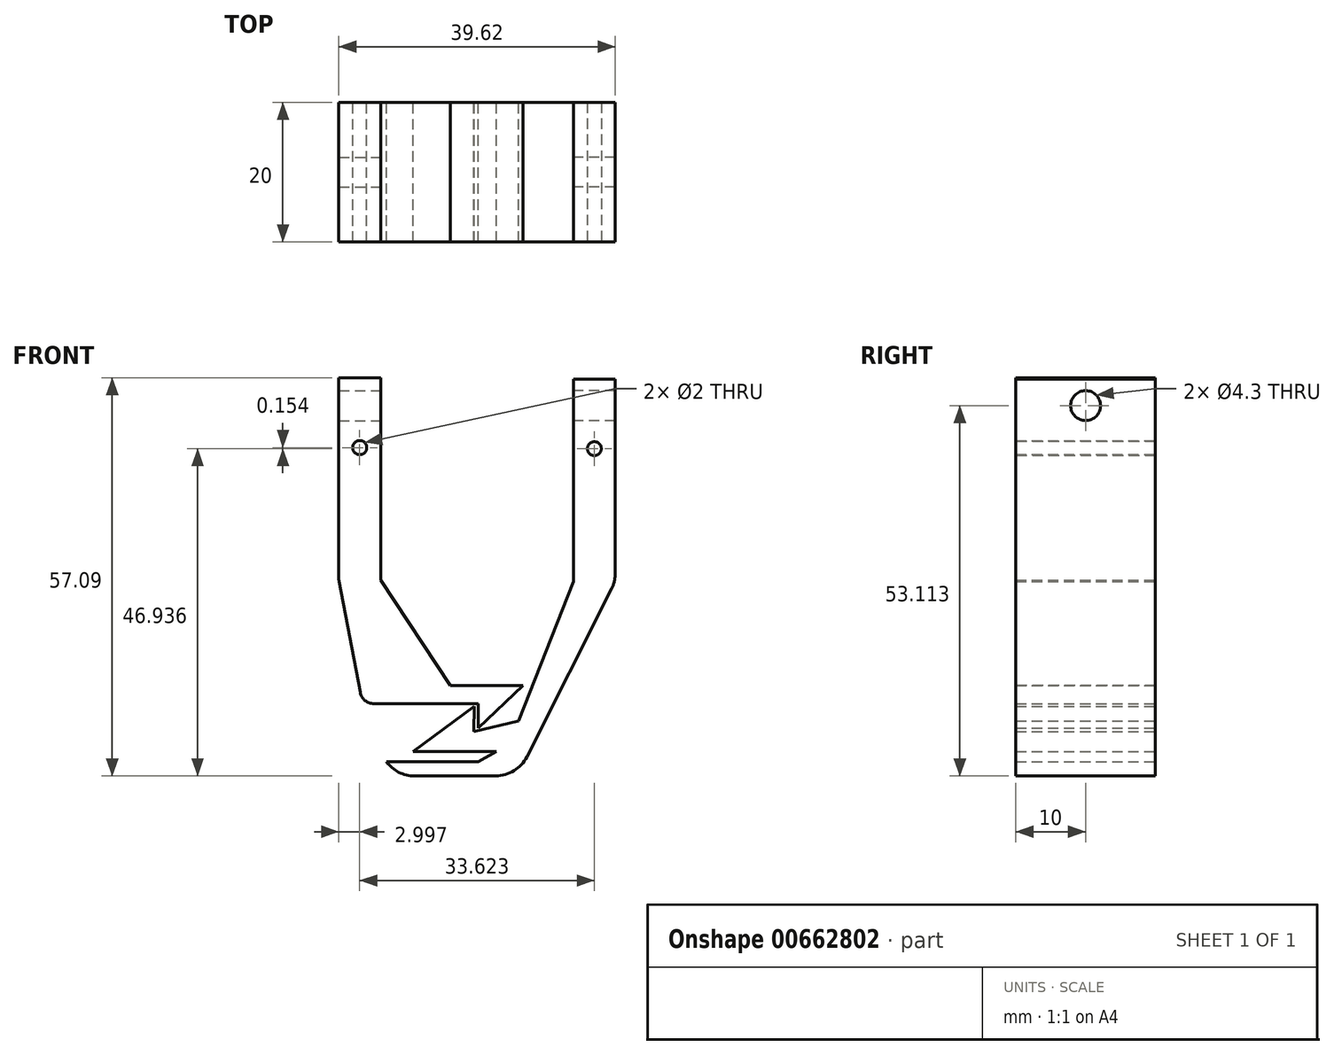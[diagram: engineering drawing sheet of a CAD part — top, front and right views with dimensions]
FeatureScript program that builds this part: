
annotation { "Feature Type Name" : "Feature", "Feature Type Description" : "" }
export const myFeature = defineFeature(function(context is Context, id is Id, definition is map)
    precondition{}
    {
        {
            var Q0;
            Q0=qCreatedBy(makeId("Front.planeOp"),FACE);
            var sketch = newSketch(context, id + "F0", { "sketchPlane" : qUnion([Q0])});
            skLineSegment(sketch, "E0.bottom", {"start": v(-14, 0) * mm, "end": v(-20, 0) * mm});
            skLineSegment(sketch, "E0.top", {"start": v(-14, 29) * mm, "end": v(-20, 29) * mm});
            skLineSegment(sketch, "E0.left", {"start": v(-14, 0) * mm, "end": v(-14, 29) * mm});
            skLineSegment(sketch, "E0.right", {"start": v(-20, 0) * mm, "end": v(-20, 29) * mm});
            skLineSegment(sketch, "E1", {"start": v(0, -15.13) * mm, "end": v(-4.04, -15.13) * mm});
            skLineSegment(sketch, "E2", {"start": v(-14, 0) * mm, "end": v(-4.04, -15.13) * mm});
            skLineSegment(sketch, "E3", {"start": v(-4.05, -17.72) * mm, "end": v(-20, 0) * mm});
            skLineSegment(sketch, "E4", {"start": v(-4.05, -17.72) * mm, "end": v(0, -17.72) * mm});
            skLineSegment(sketch, "E5", {"start": v(0, -17.72) * mm, "end": v(0, -21.21) * mm});
            skLineSegment(sketch, "E6", {"start": v(0, -15.13) * mm, "end": v(6.4, -15.13) * mm});
            skLineSegment(sketch, "E7", {"start": v(6.4, -15.13) * mm, "end": v(0, -21.21) * mm});
            skLineSegment(sketch, "E8", {"start": v(-20, 0) * mm, "end": v(-16.63, -17.72) * mm});
            skLineSegment(sketch, "E9", {"start": v(-16.63, -17.72) * mm, "end": v(-4.05, -17.72) * mm});
            skPoint(sketch, "E10", {"position": v(-17, 19) * mm});
            skSolve(sketch);
        }
        {
            var Q0;
            Q0=qSketchRegion(id+"F0",true);
            extrude(context, id + "F1", {"entities" : qUnion([Q0]), "depth" : 20 * mm, "offsetDistance" : 25 * mm, "symmetric" : true});
        }
        {
            var Q0;
            Q0=qCreatedBy(makeId("Front.planeOp"),FACE);
            var sketch = newSketch(context, id + "F2", { "sketchPlane" : qUnion([Q0])});
            skLineSegment(sketch, "E11.MirrorCS", {"start": v(19.62, -0.19) * mm, "end": v(19.62, 26.84) * mm});
            skLineSegment(sketch, "E12.MirrorCS", {"start": v(13.62, -0.19) * mm, "end": v(13.62, 26.84) * mm});
            skLineSegment(sketch, "E13.MirrorCS", {"start": v(13.62, -0.19) * mm, "end": v(19.62, -0.19) * mm});
            skLineSegment(sketch, "E14", {"start": v(5.79, -20.18) * mm, "end": v(-0.63, -21.74) * mm});
            skLineSegment(sketch, "E15", {"start": v(5.79, -20.18) * mm, "end": v(5.79, -24.57) * mm});
            skLineSegment(sketch, "E16", {"start": v(5.79, -24.57) * mm, "end": v(-0.66, -24.57) * mm});
            skLineSegment(sketch, "E17", {"start": v(-0.66, -24.57) * mm, "end": v(-0.62, -20.18) * mm});
            skLineSegment(sketch, "E18", {"start": v(-0.62, -18.1) * mm, "end": v(-0.63, -21.74) * mm});
            skLineSegment(sketch, "E19", {"start": v(13.62, -0.19) * mm, "end": v(5.79, -20.18) * mm});
            skLineSegment(sketch, "E20", {"start": v(-0.66, -24.57) * mm, "end": v(-9.38, -24.57) * mm});
            skLineSegment(sketch, "E21", {"start": v(-9.38, -24.57) * mm, "end": v(-0.62, -18.1) * mm});
            skLineSegment(sketch, "E22", {"start": v(5.56, -28.09) * mm, "end": v(-13.19, -28.09) * mm});
            skLineSegment(sketch, "E23", {"start": v(-13.19, -28.09) * mm, "end": v(-13.19, -26.04) * mm});
            skLineSegment(sketch, "E24", {"start": v(-13.19, -26.04) * mm, "end": v(0, -26.04) * mm});
            skLineSegment(sketch, "E25", {"start": v(0, -26.04) * mm, "end": v(2.57, -24.57) * mm});
            skLineSegment(sketch, "E26", {"start": v(19.62, 26.84) * mm, "end": v(19.62, 28.85) * mm});
            skLineSegment(sketch, "E27", {"start": v(13.62, 26.84) * mm, "end": v(13.62, 28.85) * mm});
            skLineSegment(sketch, "E28", {"start": v(13.62, 28.85) * mm, "end": v(19.62, 28.85) * mm});
            skPoint(sketch, "E29", {"position": v(16.62, 18.85) * mm});
            skLineSegment(sketch, "E30", {"start": v(19.62, -0.19) * mm, "end": v(5.56, -28.09) * mm});
            skLineSegment(sketch, "E31", {"start": v(16.62, 28.85) * mm, "end": v(16.62, 22.82) * mm});
            skSolve(sketch);
        }
        {
            var Q0;
            Q0 = qSketchRegion(id + "F2", true);
            extrude(context, id + "F3", {"entities" : qUnion([Q0]), "depth" : 20 * mm, "offsetDistance" : 25 * mm, "symmetric" : true});
        }
        {
            var Q0;
            Q0=makeQuery(id+"F3.opExtrude","SWEPT_EDGE",EDGE,{"disambiguationData":[OSD([sQuery(id+"F2.wireOp",EDGE,"du4RMWLr-ao0C-ay0E-4CYy-pwUNnrK6PciY"),sQuery(id+"F2.wireOp",EDGE,"E22")])]});
            fillet(context, id + "F4", {"entities" : qUnion([Q0]), "radius" : 5 * mm, "tangentPropagation" : true, "allowEdgeOverflow" : false});
        }
        {
            var Q0;
            Q0=makeQuery(id+"F1.opExtrude","SWEPT_EDGE",EDGE,{"disambiguationData":[OSD([sQuery(id+"F0.wireOp",EDGE,"E8"),sQuery(id+"F0.wireOp",EDGE,"E9")])]});
            fillet(context, id + "F5", {"entities" : qUnion([Q0]), "radius" : 2 * mm, "tangentPropagation" : true, "allowEdgeOverflow" : false});
        }
        {
            var Q0;
            Q0=makeQuery(id+"F1.opExtrude","SWEPT_EDGE",EDGE,{"disambiguationData":[OSD([sQuery(id+"F0.wireOp",EDGE,"E0.bottom"),sQuery(id+"F0.wireOp",EDGE,"E0.right"),sQuery(id+"F0.wireOp",EDGE,"E3"),sQuery(id+"F0.wireOp",EDGE,"E8")])]});
            fillet(context, id + "F6", {"entities" : qUnion([Q0]), "radius" : 2 * mm, "tangentPropagation" : true, "allowEdgeOverflow" : false});
        }
        {
            var Q0;
            Q0=makeQuery(id+"F3.opExtrude","SWEPT_EDGE",EDGE,{"disambiguationData":[OSD([sQuery(id+"F2.wireOp",EDGE,"E11.MirrorCS"),sQuery(id+"F2.wireOp",EDGE,"E13.MirrorCS"),sQuery(id+"F2.wireOp",EDGE,"409ef352-82fb-4545-b7b6-5d9b69b97d5a")])]});
            fillet(context, id + "F7", {"entities" : qUnion([Q0]), "radius" : 5 * mm, "tangentPropagation" : true, "allowEdgeOverflow" : false});
        }
        {
            var Q0;
            Q0=qCreatedBy(makeId("Right.planeOp"),FACE);
            var sketch = newSketch(context, id + "F8", { "sketchPlane" : qUnion([Q0])});
            skPoint(sketch, "E32", {"position": v(0, 25.02) * mm});
            skSolve(sketch);
        }
        {
            var Q0;
            Q0=sQuery(id+"F8.wireOp",VERTEX,"E32");
            var Q1;
            Q1=makeQuery(id+"F3.opExtrude","SWEPT_BODY",BODY,{"disambiguationData":[OSD([sQuery(id+"F2.wireOp",EDGE,"E11.MirrorCS"),sQuery(id+"F2.wireOp",EDGE,"E12.MirrorCS"),sQuery(id+"F2.wireOp",EDGE,"E14"),sQuery(id+"F2.wireOp",EDGE,"E16"),sQuery(id+"F2.wireOp",EDGE,"E18"),sQuery(id+"F2.wireOp",EDGE,"E19"),sQuery(id+"F2.wireOp",EDGE,"E20"),sQuery(id+"F2.wireOp",EDGE,"E21"),sQuery(id+"F2.wireOp",EDGE,"409ef352-82fb-4545-b7b6-5d9b69b97d5a"),sQuery(id+"F2.wireOp",EDGE,"du4RMWLr-ao0C-ay0E-4CYy-pwUNnrK6PciY"),sQuery(id+"F2.wireOp",EDGE,"E22"),sQuery(id+"F2.wireOp",EDGE,"E23"),sQuery(id+"F2.wireOp",EDGE,"E24"),sQuery(id+"F2.wireOp",EDGE,"E25"),sQuery(id+"F2.wireOp",EDGE,"E26"),sQuery(id+"F2.wireOp",EDGE,"E27"),sQuery(id+"F2.wireOp",EDGE,"E28")])]});
            hole(context, id + "F9", {"style" : HoleStyle.SIMPLE, "endStyle" : HoleEndStyle.THROUGH, "oppositeDirection" : true, "holeDiameter" : 4.3 * mm, "majorDiameter" : 5 * mm, "isTappedThrough" : true, "tappedDepth" : 12 * mm, "tapClearance" : 3, "locations" : qUnion([Q0]), "scope" : qUnion([Q1])});
        }
        {
            var Q0;
            Q0=sQuery(id+"F8.wireOp",VERTEX,"E32");
            var Q1;
            Q1=makeQuery(id+"F1.opExtrude","SWEPT_BODY",BODY,{"disambiguationData":[OSD([sQuery(id+"F0.wireOp",EDGE,"E0.top"),sQuery(id+"F0.wireOp",EDGE,"E0.left"),sQuery(id+"F0.wireOp",EDGE,"E0.right"),sQuery(id+"F0.wireOp",EDGE,"E1"),sQuery(id+"F0.wireOp",EDGE,"E2"),sQuery(id+"F0.wireOp",EDGE,"E4"),sQuery(id+"F0.wireOp",EDGE,"E5"),sQuery(id+"F0.wireOp",EDGE,"E6"),sQuery(id+"F0.wireOp",EDGE,"E7"),sQuery(id+"F0.wireOp",EDGE,"E8"),sQuery(id+"F0.wireOp",EDGE,"E9")])]});
            hole(context, id + "F10", {"style" : HoleStyle.SIMPLE, "endStyle" : HoleEndStyle.THROUGH, "holeDiameter" : 4.3 * mm, "majorDiameter" : 5 * mm, "isTappedThrough" : true, "tappedDepth" : 12 * mm, "tapClearance" : 3, "locations" : qUnion([Q0]), "scope" : qUnion([Q1])});
        }
        {
            var Q0;
            Q0=sQuery(id+"F0.wireOp",VERTEX,"E10");
            var Q1;
            Q1=makeQuery(id+"F1.opExtrude","SWEPT_BODY",BODY,{"disambiguationData":[OSD([sQuery(id+"F0.wireOp",EDGE,"E0.top"),sQuery(id+"F0.wireOp",EDGE,"E0.left"),sQuery(id+"F0.wireOp",EDGE,"E0.right"),sQuery(id+"F0.wireOp",EDGE,"E1"),sQuery(id+"F0.wireOp",EDGE,"E2"),sQuery(id+"F0.wireOp",EDGE,"E4"),sQuery(id+"F0.wireOp",EDGE,"E5"),sQuery(id+"F0.wireOp",EDGE,"E6"),sQuery(id+"F0.wireOp",EDGE,"E7"),sQuery(id+"F0.wireOp",EDGE,"E8"),sQuery(id+"F0.wireOp",EDGE,"E9")])]});
            hole(context, id + "F11", {"style" : HoleStyle.SIMPLE, "endStyle" : HoleEndStyle.THROUGH, "oppositeDirection" : true, "holeDiameter" : 2 * mm, "majorDiameter" : 5 * mm, "isTappedThrough" : true, "tappedDepth" : 12 * mm, "tapClearance" : 3, "locations" : qUnion([Q0]), "scope" : qUnion([Q1])});
        }
        {
            var Q0;
            Q0=sQuery(id+"F0.wireOp",VERTEX,"E10");
            var Q1;
            Q1=makeQuery(id+"F1.opExtrude","SWEPT_BODY",BODY,{"disambiguationData":[OSD([sQuery(id+"F0.wireOp",EDGE,"E0.top"),sQuery(id+"F0.wireOp",EDGE,"E0.left"),sQuery(id+"F0.wireOp",EDGE,"E0.right"),sQuery(id+"F0.wireOp",EDGE,"E1"),sQuery(id+"F0.wireOp",EDGE,"E2"),sQuery(id+"F0.wireOp",EDGE,"E4"),sQuery(id+"F0.wireOp",EDGE,"E5"),sQuery(id+"F0.wireOp",EDGE,"E6"),sQuery(id+"F0.wireOp",EDGE,"E7"),sQuery(id+"F0.wireOp",EDGE,"E8"),sQuery(id+"F0.wireOp",EDGE,"E9")])]});
            hole(context, id + "F12", {"style" : HoleStyle.SIMPLE, "endStyle" : HoleEndStyle.THROUGH, "holeDiameter" : 2 * mm, "majorDiameter" : 5 * mm, "isTappedThrough" : true, "tappedDepth" : 12 * mm, "tapClearance" : 3, "locations" : qUnion([Q0]), "scope" : qUnion([Q1])});
        }
        {
            var Q0;
            Q0=sQuery(id+"F2.wireOp",VERTEX,"E29");
            var Q1;
            Q1=makeQuery(id+"F3.opExtrude","SWEPT_BODY",BODY,{"disambiguationData":[OSD([sQuery(id+"F2.wireOp",EDGE,"E11.MirrorCS"),sQuery(id+"F2.wireOp",EDGE,"E12.MirrorCS"),sQuery(id+"F2.wireOp",EDGE,"E14"),sQuery(id+"F2.wireOp",EDGE,"E16"),sQuery(id+"F2.wireOp",EDGE,"E18"),sQuery(id+"F2.wireOp",EDGE,"E19"),sQuery(id+"F2.wireOp",EDGE,"E20"),sQuery(id+"F2.wireOp",EDGE,"E21"),sQuery(id+"F2.wireOp",EDGE,"409ef352-82fb-4545-b7b6-5d9b69b97d5a"),sQuery(id+"F2.wireOp",EDGE,"du4RMWLr-ao0C-ay0E-4CYy-pwUNnrK6PciY"),sQuery(id+"F2.wireOp",EDGE,"E22"),sQuery(id+"F2.wireOp",EDGE,"E23"),sQuery(id+"F2.wireOp",EDGE,"E24"),sQuery(id+"F2.wireOp",EDGE,"E25"),sQuery(id+"F2.wireOp",EDGE,"E26"),sQuery(id+"F2.wireOp",EDGE,"E27"),sQuery(id+"F2.wireOp",EDGE,"E28")])]});
            var Q2;
            Q2=makeQuery(id+"F3.opExtrude","SWEPT_BODY",BODY,{"disambiguationData":[OSD([sQuery(id+"F2.wireOp",EDGE,"E11.MirrorCS"),sQuery(id+"F2.wireOp",EDGE,"E12.MirrorCS"),sQuery(id+"F2.wireOp",EDGE,"E14"),sQuery(id+"F2.wireOp",EDGE,"E16"),sQuery(id+"F2.wireOp",EDGE,"E18"),sQuery(id+"F2.wireOp",EDGE,"E19"),sQuery(id+"F2.wireOp",EDGE,"E20"),sQuery(id+"F2.wireOp",EDGE,"E21"),sQuery(id+"F2.wireOp",EDGE,"409ef352-82fb-4545-b7b6-5d9b69b97d5a"),sQuery(id+"F2.wireOp",EDGE,"du4RMWLr-ao0C-ay0E-4CYy-pwUNnrK6PciY"),sQuery(id+"F2.wireOp",EDGE,"E22"),sQuery(id+"F2.wireOp",EDGE,"E23"),sQuery(id+"F2.wireOp",EDGE,"E24"),sQuery(id+"F2.wireOp",EDGE,"E25"),sQuery(id+"F2.wireOp",EDGE,"E26"),sQuery(id+"F2.wireOp",EDGE,"E27"),sQuery(id+"F2.wireOp",EDGE,"E28")])]});
            hole(context, id + "F13", {"style" : HoleStyle.SIMPLE, "endStyle" : HoleEndStyle.THROUGH, "holeDiameter" : 2 * mm, "majorDiameter" : 5 * mm, "isTappedThrough" : true, "tappedDepth" : 12 * mm, "tapClearance" : 3, "locations" : qUnion([Q0]), "scope" : qUnion([Q1, Q2])});
        }
        {
            var Q0;
            Q0=sQuery(id+"F2.wireOp",VERTEX,"E29");
            var Q1;
            Q1=makeQuery(id+"F3.opExtrude","SWEPT_BODY",BODY,{"disambiguationData":[OSD([sQuery(id+"F2.wireOp",EDGE,"E11.MirrorCS"),sQuery(id+"F2.wireOp",EDGE,"E12.MirrorCS"),sQuery(id+"F2.wireOp",EDGE,"E14"),sQuery(id+"F2.wireOp",EDGE,"E16"),sQuery(id+"F2.wireOp",EDGE,"E18"),sQuery(id+"F2.wireOp",EDGE,"E19"),sQuery(id+"F2.wireOp",EDGE,"E20"),sQuery(id+"F2.wireOp",EDGE,"E21"),sQuery(id+"F2.wireOp",EDGE,"409ef352-82fb-4545-b7b6-5d9b69b97d5a"),sQuery(id+"F2.wireOp",EDGE,"du4RMWLr-ao0C-ay0E-4CYy-pwUNnrK6PciY"),sQuery(id+"F2.wireOp",EDGE,"E22"),sQuery(id+"F2.wireOp",EDGE,"E23"),sQuery(id+"F2.wireOp",EDGE,"E24"),sQuery(id+"F2.wireOp",EDGE,"E25"),sQuery(id+"F2.wireOp",EDGE,"E26"),sQuery(id+"F2.wireOp",EDGE,"E27"),sQuery(id+"F2.wireOp",EDGE,"E28")])]});
            hole(context, id + "F14", {"style" : HoleStyle.SIMPLE, "endStyle" : HoleEndStyle.THROUGH, "oppositeDirection" : true, "holeDiameter" : 2 * mm, "majorDiameter" : 5 * mm, "isTappedThrough" : true, "tappedDepth" : 12 * mm, "tapClearance" : 3, "locations" : qUnion([Q0]), "scope" : qUnion([Q1])});
        }
    });
